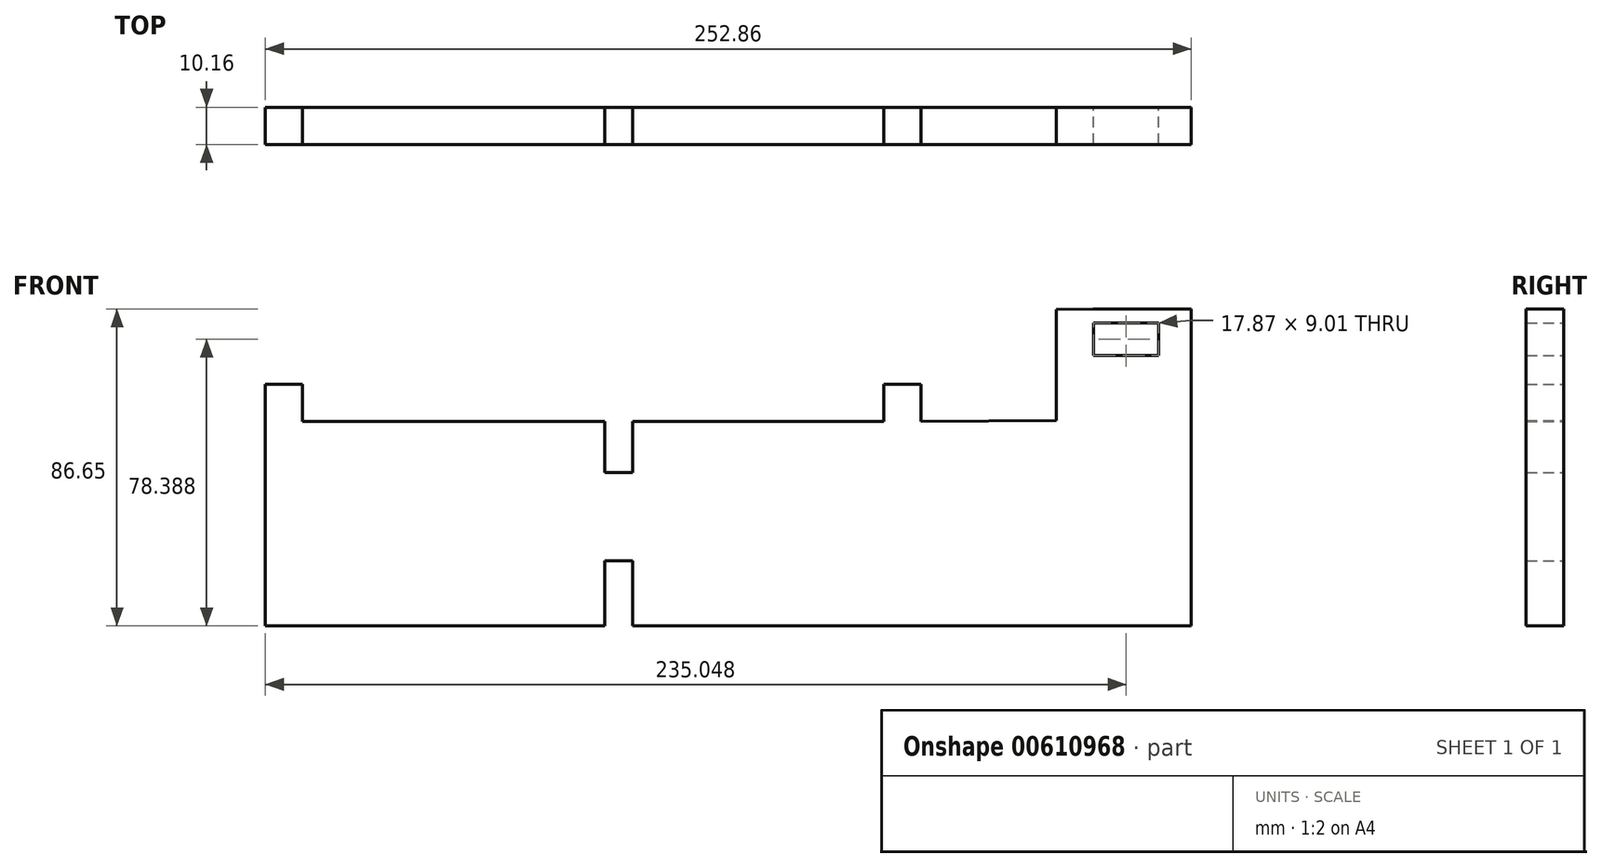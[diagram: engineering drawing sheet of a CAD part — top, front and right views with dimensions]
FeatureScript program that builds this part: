
annotation { "Feature Type Name" : "Feature", "Feature Type Description" : "" }
export const myFeature = defineFeature(function(context is Context, id is Id, definition is map)
    precondition{}
    {
        {
            var Q0;
            Q0=qCreatedBy(makeId("Front.planeOp"),FACE);
            var sketch = newSketch(context, id + "F0", { "sketchPlane" : qUnion([Q0])});
            skLineSegment(sketch, "E0", {"start": v(12.52, 11.37) * mm, "end": v(-134.8, 11.37) * mm});
            skLineSegment(sketch, "E1", {"start": v(-134.8, 11.37) * mm, "end": v(-134.8, 29.14) * mm});
            skLineSegment(sketch, "E2", {"start": v(-134.8, 29.14) * mm, "end": v(-142.42, 29.14) * mm});
            skLineSegment(sketch, "E3", {"start": v(-142.42, 29.14) * mm, "end": v(-142.42, 11.37) * mm});
            skLineSegment(sketch, "E4", {"start": v(-142.42, 11.37) * mm, "end": v(-235.15, 11.37) * mm});
            skLineSegment(sketch, "E5", {"start": v(-235.15, 11.37) * mm, "end": v(-235.15, 77.43) * mm});
            skLineSegment(sketch, "E6", {"start": v(-235.15, 77.43) * mm, "end": v(-225, 77.43) * mm});
            skLineSegment(sketch, "E7", {"start": v(-225, 77.43) * mm, "end": v(-225, 67.26) * mm});
            skLineSegment(sketch, "E8", {"start": v(-225, 67.26) * mm, "end": v(-142.42, 67.26) * mm});
            skLineSegment(sketch, "E9", {"start": v(-142.42, 67.26) * mm, "end": v(-142.42, 53.28) * mm});
            skLineSegment(sketch, "E10", {"start": v(-142.42, 53.28) * mm, "end": v(-134.8, 53.28) * mm});
            skLineSegment(sketch, "E11", {"start": v(-134.8, 53.28) * mm, "end": v(-134.8, 67.26) * mm});
            skLineSegment(sketch, "E12", {"start": v(-134.8, 67.26) * mm, "end": v(-66.21, 67.26) * mm});
            skLineSegment(sketch, "E13", {"start": v(-66.21, 67.26) * mm, "end": v(-66.21, 77.43) * mm});
            skLineSegment(sketch, "E14", {"start": v(-66.21, 77.43) * mm, "end": v(-56.05, 77.43) * mm});
            skLineSegment(sketch, "E15", {"start": v(-56.05, 77.43) * mm, "end": v(-56.05, 67.26) * mm});
            skLineSegment(sketch, "E16", {"start": v(-56.05, 67.26) * mm, "end": v(-19.21, 67.49) * mm});
            skLineSegment(sketch, "E17", {"start": v(-19.21, 67.49) * mm, "end": v(-19.21, 97.9) * mm});
            skLineSegment(sketch, "E18", {"start": v(-19.21, 97.9) * mm, "end": v(-9.06, 97.97) * mm});
            skLineSegment(sketch, "E19", {"start": v(-9.06, 97.97) * mm, "end": v(-9.03, 94.15) * mm});
            skLineSegment(sketch, "E20", {"start": v(-9.03, 94.15) * mm, "end": v(-8.98, 85.25) * mm});
            skLineSegment(sketch, "E21", {"start": v(-8.98, 85.25) * mm, "end": v(8.83, 85.36) * mm});
            skLineSegment(sketch, "E22", {"start": v(-9.03, 94.15) * mm, "end": v(8.83, 94.26) * mm});
            skLineSegment(sketch, "E23", {"start": v(8.83, 94.26) * mm, "end": v(8.83, 85.36) * mm});
            skLineSegment(sketch, "E24", {"start": v(8.83, 94.26) * mm, "end": v(8.8, 97.97) * mm});
            skLineSegment(sketch, "E25", {"start": v(8.8, 97.97) * mm, "end": v(-9.06, 97.97) * mm});
            skLineSegment(sketch, "E26", {"start": v(8.8, 97.97) * mm, "end": v(17.71, 98.02) * mm});
            skLineSegment(sketch, "E27", {"start": v(17.71, 98.02) * mm, "end": v(17.71, 11.37) * mm});
            skLineSegment(sketch, "E28", {"start": v(17.71, 11.37) * mm, "end": v(12.52, 11.37) * mm});
            skSolve(sketch);
        }
        {
            var Q0;
            Q0=makeQuery(id+"F0.imprint","IMPRINT",FACE,{"disambiguationData":[TD([[makeQuery(id+"F0.imprint","IMPRINT",EDGE,{"derivedFrom":sQuery(id+"F0.wireOp",EDGE,"E0")}),-1.0]])]});
            var Q1;
            Q1=makeQuery(id+"F0.imprint","IMPRINT",FACE,{"disambiguationData":[TD([[makeQuery(id+"F0.imprint","IMPRINT",EDGE,{"derivedFrom":sQuery(id+"F0.wireOp",EDGE,"E19")}),1.0]])]});
            extrude(context, id + "F1", {"entities" : qUnion([Q0, Q1]), "depth" : 10.16 * mm, "offsetDistance" : 25.4 * mm});
        }
    });
